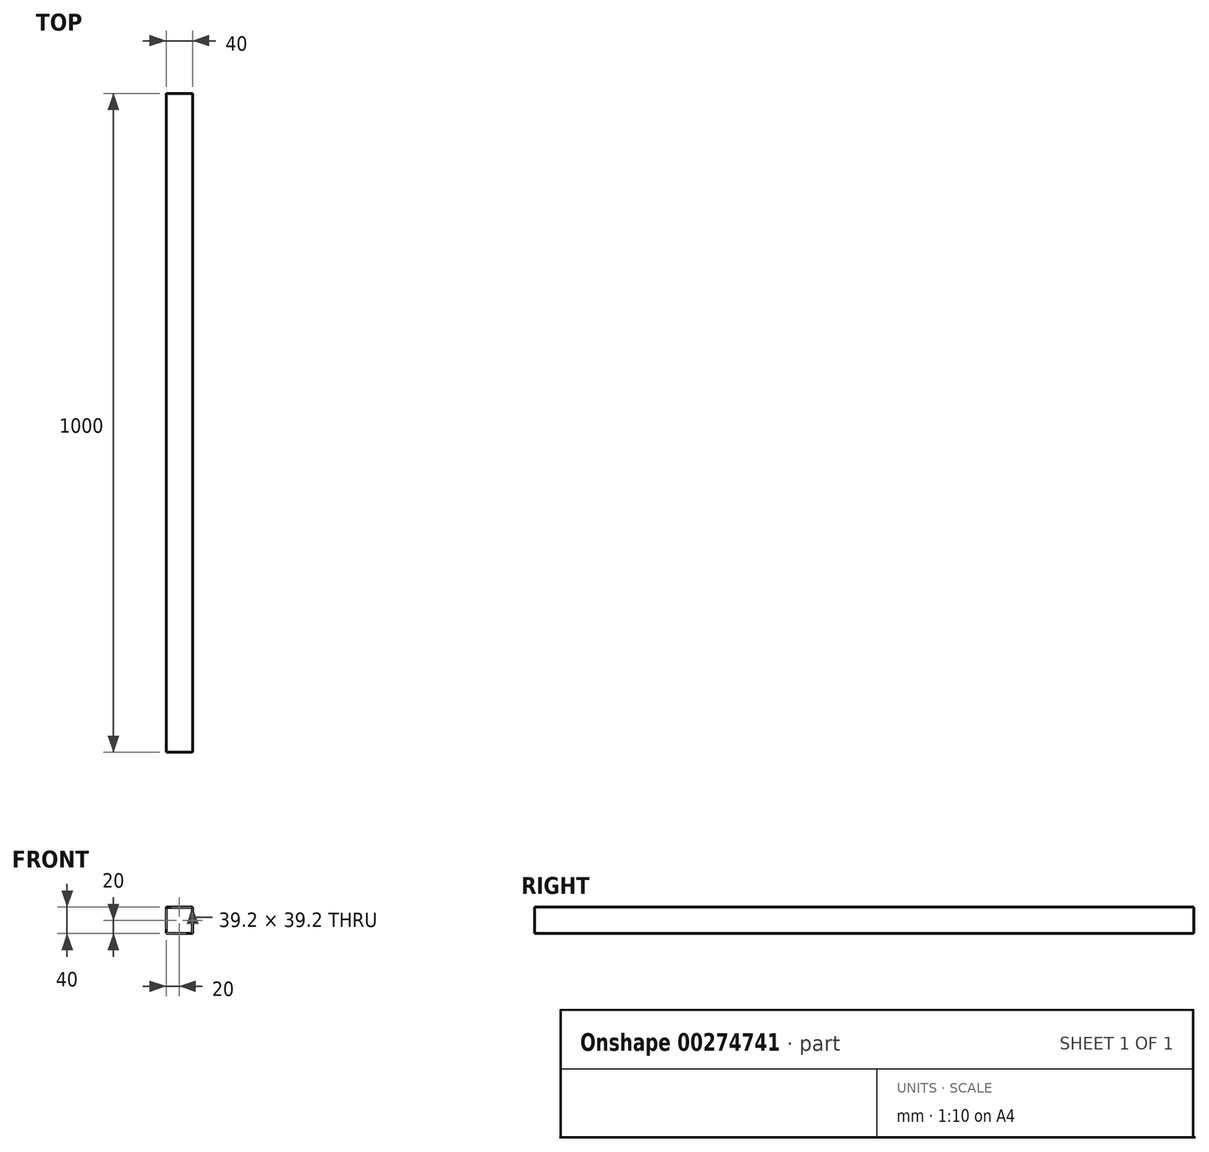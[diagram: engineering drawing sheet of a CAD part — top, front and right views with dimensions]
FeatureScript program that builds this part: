
annotation { "Feature Type Name" : "Feature", "Feature Type Description" : "" }
export const myFeature = defineFeature(function(context is Context, id is Id, definition is map)
    precondition{}
    {
        {
            var Q0;
            Q0=qCreatedBy(makeId("Front.planeOp"),FACE);
            var sketch = newSketch(context, id + "F0", { "sketchPlane" : qUnion([Q0])});
            skLineSegment(sketch, "E0.bottom", {"start": v(20, -20) * mm, "end": v(-20, -20) * mm});
            skLineSegment(sketch, "E0.top", {"start": v(20, 20) * mm, "end": v(-20, 20) * mm});
            skLineSegment(sketch, "E0.left", {"start": v(20, -20) * mm, "end": v(20, 20) * mm});
            skLineSegment(sketch, "E0.right", {"start": v(-20, -20) * mm, "end": v(-20, 20) * mm});
            skPoint(sketch, "E0.middle", {"position": v(0, 0) * mm});
            skLineSegment(sketch, "E1.bottom", {"start": v(19.6, -19.6) * mm, "end": v(-19.6, -19.6) * mm});
            skLineSegment(sketch, "E1.top", {"start": v(19.6, 19.6) * mm, "end": v(-19.6, 19.6) * mm});
            skLineSegment(sketch, "E1.left", {"start": v(19.6, -19.6) * mm, "end": v(19.6, 19.6) * mm});
            skLineSegment(sketch, "E1.right", {"start": v(-19.6, -19.6) * mm, "end": v(-19.6, 19.6) * mm});
            skSolve(sketch);
        }
        {
            var Q0;
            Q0=makeQuery(id+"F0.imprint","IMPRINT",FACE,{"disambiguationData":[TD([[makeQuery(id+"F0.imprint","IMPRINT",EDGE,{"derivedFrom":sQuery(id+"F0.wireOp",EDGE,"E0.bottom")}),-1.0]])]});
            extrude(context, id + "F1", {"entities" : qUnion([Q0]), "depth" : 1000 * mm});
        }
    });
